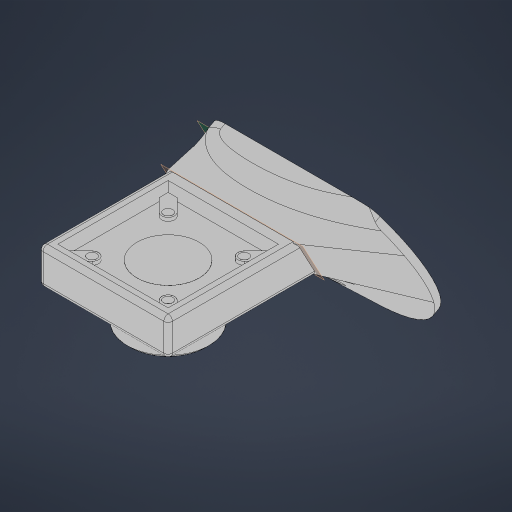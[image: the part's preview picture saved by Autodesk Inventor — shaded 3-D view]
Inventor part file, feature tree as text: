
AUTODESK INVENTOR PART (.ipt)
format: ipt  version: 2023 (Build 270158000, 158)  size: 492,032 bytes
history: native  units: in
note: dims shown in document units (in); Inventor stores cm internally (conversion verified against a paired STEP export)
features: sketch x10, extrude x7, hole x3, fillet x3, plane x2, other x2, projected_geometry x2, loft x1, chamfer x1
ambient origin geometry x8: Origin, YZ Plane, XZ Plane, XY Plane, X Axis, Y Axis, Z Axis, Center Point
bodies: Solid1 (feature_tree)
feature tree (31):
  extrude  "Extrusion1"  Depth=0.525in
  extrude  "Extrusion2"  Depth=0.4252in
  plane  "Work Plane1"
  extrude  "Extrusion3"  Depth=0.6in
  loft  "Loft1"
  extrude  "Extrusion4"  TaperAngle=0.0deg  [1 undecoded]
  hole  "Hole1"  [1 undecoded]
  extrude  "Extrusion5"  Depth=1.1875in
  extrude  "Extrusion6"  Depth=0.1839in
  hole  "Hole2"  [1 undecoded]
  plane  "Work Plane2"
  hole  "Hole3"  [1 undecoded]
  fillet  "Fillet1"  Radius=0.9792in
  chamfer  "Chamfer1"  Angle=30.0deg  [1 undecoded]
  fillet  "Fillet2"  Radius=0.3in
  extrude  "Extrusion7"  Depth=0.2in
  fillet  "Fillet3"  Radius=0.0625in
  sketch  "Sketch1"  dims[d0=1.875in d1=0.525in]
  sketch  "Sketch2"  dims[d2=1.875in d3=0.0in d4=0.4252in]
  sketch  "Sketch3"  dims[d5=1.875in d6=0.0in d7=0.6in]
  other  "Edges1"
  other  "Edges2"
  sketch  "Sketch4"  dims[d9=3.0in d10=0.1in d11=0.0in]
  projected_geometry  "Projected Loop1"
  sketch  "Sketch5"  dims[d12=0.0in d13=90.0deg d14=0.0in d15=90.0deg]
  sketch  "Sketch6"  dims[d16=1.6in d17=0.2in d18=0.0in]
  sketch  "Sketch7"  dims[d19=0.9in d20=0.75in d21=0.119in d22=0.25in d23=0.6871in d24=1.0in d25=0.8108in d26=1.1875in]
  projected_geometry  "Projected Loop2"
  sketch  "Sketch8"  dims[d27=0.5in d28=0.0in d29=0.1839in]
  sketch  "Sketch9"  dims[d30=1.1024in d31=0.05in d32=0.0in]
  sketch  "Sketch10"  dims[d33=0.1339in d34=0.75in d35=0.185in d36=0.25in d37=0.6871in d38=1.0in d39=0.8108in d40=0.9792in d41=0.9792in d42=30.0deg d43=0.3in d44=0.2in d45=0.177in d46=0.75in d47=0.313in d48=0.45in d49=0.5635in d50=1.0in d51=0.8108in d52=0.0625in d53=0.05in d54=0.125in d55=45.0deg d56=0.0625in d57=1.0in d58=1.0in d59=0.0in d60=0.25in]
note: 5 required parameter values undecoded (feature->parameter linkage not recoverable at this tier; creation-order binding heuristic only, values carry confidence <= 0.55)
